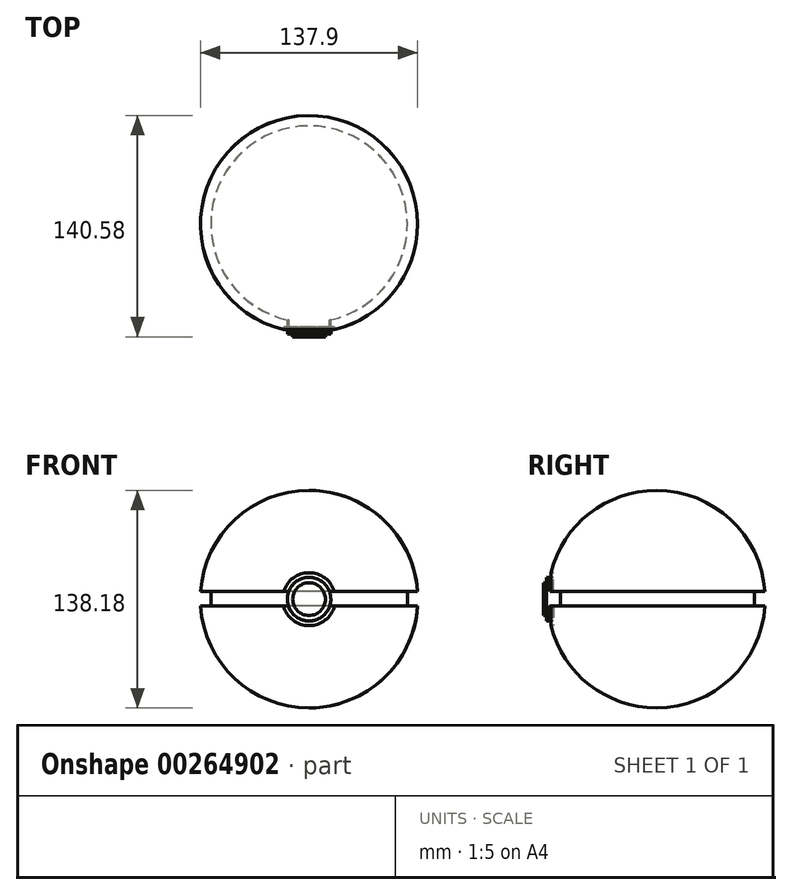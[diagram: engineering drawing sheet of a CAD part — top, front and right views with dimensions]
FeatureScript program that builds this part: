
annotation { "Feature Type Name" : "Feature", "Feature Type Description" : "" }
export const myFeature = defineFeature(function(context is Context, id is Id, definition is map)
    precondition{}
    {
        {
            var Q0;
            Q0=qCreatedBy(makeId("Front.planeOp"),FACE);
            var sketch = newSketch(context, id + "F0", { "sketchPlane" : qUnion([Q0])});
            skArc(sketch, "E0", {"start": v(0, -69.09) * mm, "mid": v(47.28, -50.38) * mm, "end": v(68.95, -4.39) * mm});
            skLineSegment(sketch, "E1", {"start": v(0, 69.09) * mm, "end": v(0, -69.09) * mm});
            skLineSegment(sketch, "E2", {"start": v(68.91, 4.96) * mm, "end": v(62.4, 4.96) * mm});
            skLineSegment(sketch, "E3", {"start": v(62.4, 4.96) * mm, "end": v(62.4, -4.39) * mm});
            skLineSegment(sketch, "E4", {"start": v(62.4, -4.39) * mm, "end": v(68.95, -4.39) * mm});
            skArc(sketch, "E5.trimOffspring", {"start": v(68.91, 4.96) * mm, "mid": v(47.07, 50.58) * mm, "end": v(0, 69.09) * mm});
            skSolve(sketch);
        }
        {
            var Q0;
            Q0=makeQuery(id+"F0.imprint","IMPRINT",FACE,{"disambiguationData":[TD([[makeQuery(id+"F0.imprint","IMPRINT",EDGE,{"derivedFrom":sQuery(id+"F0.wireOp",EDGE,"E0")}),1.0]])]});
            var Q1;
            Q1=sQuery(id+"F0.wireOp",EDGE,"E1");
            revolve(context, id + "F1", {"entities" : qUnion([Q0]), "axis" : qUnion([Q1]), "revolveType" : RevolveType.FULL});
        }
        {
            var Q0;
            Q0=qCreatedBy(makeId("Front.planeOp"),FACE);
            var sketch = newSketch(context, id + "F2", { "sketchPlane" : qUnion([Q0])});
            skCircle(sketch, "E6", {"center": v(0, 0) * mm, "radius": 13.8 * mm});
            skSolve(sketch);
        }
        {
            var Q0;
            Q0 = qSketchRegion(id + "F2", true);
            extrude(context, id + "F3", {"entities" : qUnion([Q0]), "operationType" : NewBodyOperationType.ADD, "depth" : 69.85 * mm});
        }
        {
            var Q0;
            Q0=qCreatedBy(makeId("Front.planeOp"),FACE);
            var sketch = newSketch(context, id + "F4", { "sketchPlane" : qUnion([Q0])});
            skCircle(sketch, "E7", {"center": v(0, 0) * mm, "radius": 10.37 * mm});
            skSolve(sketch);
        }
        {
            var Q0;
            Q0 = qSketchRegion(id + "F4", true);
            extrude(context, id + "F5", {"entities" : qUnion([Q0]), "operationType" : NewBodyOperationType.ADD, "depth" : 71.63 * mm});
        }
        {
            var Q0;
            Q0=makeQuery(id+"F5.opExtrude","CAP_FACE",FACE,{"disambiguationData":[OSD([sQuery(id+"F4.wireOp",EDGE,"E7")])],"isStart":false});
            var sketch = newSketch(context, id + "F6", { "sketchPlane" : qUnion([Q0])});
            skCircle(sketch, "E8", {"center": v(0, 0) * mm, "radius": 16.81 * mm});
            skCircle(sketch, "E9", {"center": v(0, 0) * mm, "radius": 13.88 * mm});
            skSolve(sketch);
        }
        {
            var Q0;
            Q0 = qSketchRegion(id + "F6", true);
            extrude(context, id + "F7", {"entities" : qUnion([Q0]), "operationType" : NewBodyOperationType.REMOVE, "oppositeDirection" : true, "depth" : 6.35 * mm});
        }
    });
